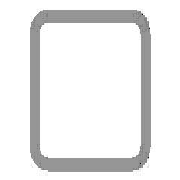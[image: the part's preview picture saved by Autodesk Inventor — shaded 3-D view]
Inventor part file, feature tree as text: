
AUTODESK INVENTOR PART (.ipt)
format: ipt  version: 2024 (Build 280153000, 153)  size: 128,512 bytes
history: native  units: mm (DEFAULTED — no unit token found)
features: other x4, extrude x1, sketch x1, plane x1
ambient origin geometry x8: Origin, YZ Plane, XZ Plane, XY Plane, X Axis, Y Axis, Z Axis, Center Point
bodies: Solid1 (feature_tree)
feature tree (7):
  parser-record x1  (decoder bookkeeping rows leaked as tree rows — omitted from the tree; the rows remain in map.json)
  other  "Driven Length"
  other  "Plano inicial"
  other  "Plano final"
  extrude  "Cuerpo"  TaperAngle=0.0deg  [1 undecoded]
  sketch  "Sketch3"  dims[d3=600.0mm d4=0.0mm d10=50.8mm d11=50.8mm d12=3.175mm d13=-0.0mm d14=600.0mm d15=25.4mm d16=25.4mm d17=6.35mm d18=90.0deg d19=600.0mm]
  plane  "Work Plane3"
note: 1 required parameter value undecoded (feature->parameter linkage not recoverable at this tier; creation-order binding heuristic only, values carry confidence <= 0.55)
